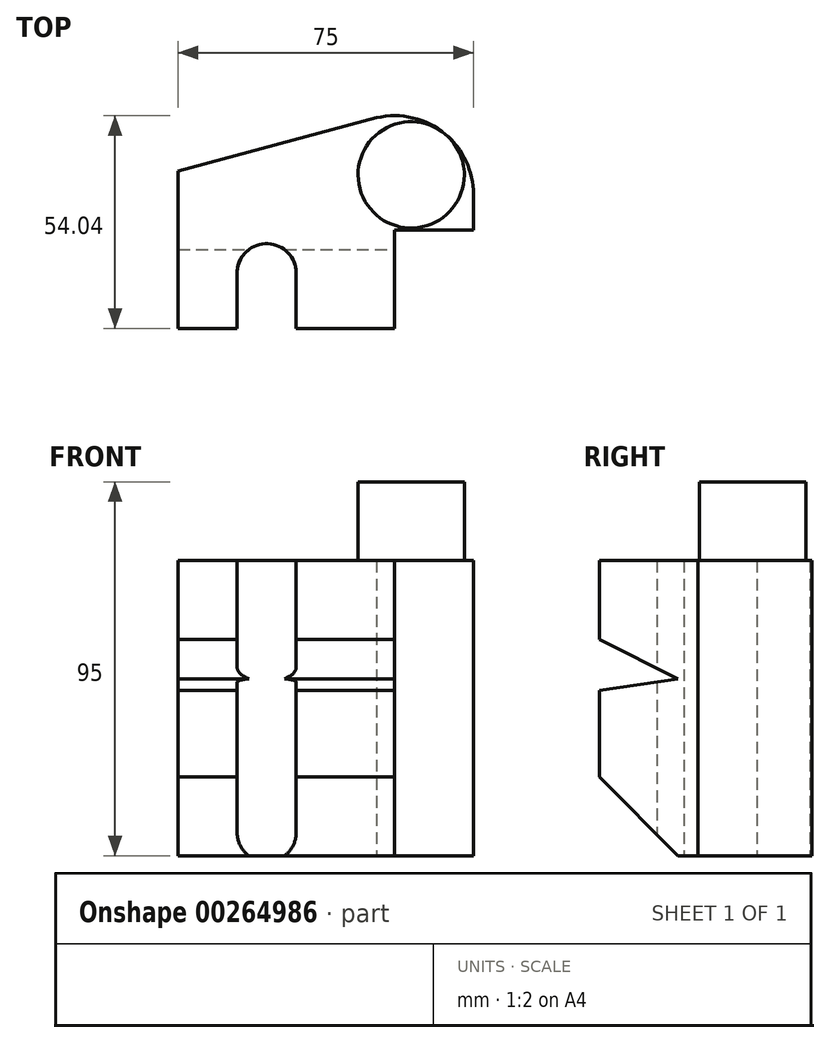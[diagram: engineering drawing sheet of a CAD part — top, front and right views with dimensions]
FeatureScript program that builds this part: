
annotation { "Feature Type Name" : "Feature", "Feature Type Description" : "" }
export const myFeature = defineFeature(function(context is Context, id is Id, definition is map)
    precondition{}
    {
        {
            var Q0;
            Q0=qCreatedBy(makeId("Top.planeOp"),FACE);
            var sketch = newSketch(context, id + "F0", { "sketchPlane" : qUnion([Q0])});
            skLineSegment(sketch, "E0", {"start": v(0, 0) * mm, "end": v(15, 0) * mm});
            skLineSegment(sketch, "E1", {"start": v(15, 0) * mm, "end": v(15, 14.68) * mm});
            skLineSegment(sketch, "E2", {"start": v(30, 14) * mm, "end": v(30, 0) * mm});
            skLineSegment(sketch, "E3", {"start": v(30, 0) * mm, "end": v(55, 0) * mm});
            skLineSegment(sketch, "E4", {"start": v(55, 0) * mm, "end": v(55, 25) * mm});
            skLineSegment(sketch, "E5", {"start": v(55, 25) * mm, "end": v(75, 25) * mm});
            skLineSegment(sketch, "E6", {"start": v(75, 25) * mm, "end": v(75, 34.04) * mm});
            skLineSegment(sketch, "E7", {"start": v(0, 0) * mm, "end": v(0, 40) * mm});
            skLineSegment(sketch, "E8", {"start": v(0, 40) * mm, "end": v(50.41, 53.5) * mm});
            skArc(sketch, "E9", {"start": v(30, 14) * mm, "mid": v(22.82, 21.5) * mm, "end": v(15, 14.68) * mm});
            skArc(sketch, "E10", {"start": v(75, 34.04) * mm, "mid": v(67.42, 49.72) * mm, "end": v(50.41, 53.5) * mm});
            skSolve(sketch);
        }
        {
            var Q0;
            Q0 = qSketchRegion(id + "F0", true);
            extrude(context, id + "F1", {"entities" : qUnion([Q0]), "depth" : 75 * mm});
        }
        {
            var Q0;
            Q0=makeQuery(id+"F1.opExtrude","CAP_FACE",FACE,{"disambiguationData":[OSD([sQuery(id+"F0.wireOp",EDGE,"E0"),sQuery(id+"F0.wireOp",EDGE,"E1"),sQuery(id+"F0.wireOp",EDGE,"E2"),sQuery(id+"F0.wireOp",EDGE,"E3"),sQuery(id+"F0.wireOp",EDGE,"E4"),sQuery(id+"F0.wireOp",EDGE,"E5"),sQuery(id+"F0.wireOp",EDGE,"E6"),sQuery(id+"F0.wireOp",EDGE,"E7"),sQuery(id+"F0.wireOp",EDGE,"E8"),sQuery(id+"F0.wireOp",EDGE,"E9"),sQuery(id+"F0.wireOp",EDGE,"E10")])],"isStart":false});
            var sketch = newSketch(context, id + "F2", { "sketchPlane" : qUnion([Q0])});
            skCircle(sketch, "E11", {"center": v(59.2, 39) * mm, "radius": 13.5 * mm});
            skSolve(sketch);
        }
        {
            var Q0;
            Q0 = qSketchRegion(id + "F2", true);
            extrude(context, id + "F3", {"entities" : qUnion([Q0]), "operationType" : NewBodyOperationType.ADD, "depth" : 20 * mm});
        }
        {
            var Q0;
            Q0=makeQuery(id+"F1.opExtrude","SWEPT_FACE",FACE,{"disambiguationData":[OSD([sQuery(id+"F0.wireOp",EDGE,"E4")])]});
            var sketch = newSketch(context, id + "F4", { "sketchPlane" : qUnion([Q0])});
            skLineSegment(sketch, "E12", {"start": v(0, 55) * mm, "end": v(20, 45) * mm});
            skLineSegment(sketch, "E13", {"start": v(20, 45) * mm, "end": v(0, 42.03) * mm});
            skLineSegment(sketch, "E14", {"start": v(0, 42.03) * mm, "end": v(0, 55) * mm});
            skSolve(sketch);
        }
        {
            var Q0;
            Q0 = qSketchRegion(id + "F4", true);
            extrude(context, id + "F5", {"entities" : qUnion([Q0]), "operationType" : NewBodyOperationType.REMOVE, "endBound" : BoundingType.THROUGH_ALL, "oppositeDirection" : true, "depth" : 25 * mm});
        }
        {
            var Q0;
            Q0=makeQuery(id+"F1.opExtrude","SWEPT_FACE",FACE,{"disambiguationData":[OSD([sQuery(id+"F0.wireOp",EDGE,"E4")])]});
            var sketch = newSketch(context, id + "F6", { "sketchPlane" : qUnion([Q0])});
            skLineSegment(sketch, "E15", {"start": v(0, 20) * mm, "end": v(20, 0) * mm});
            skLineSegment(sketch, "E16", {"start": v(20, 0) * mm, "end": v(0, 0) * mm});
            skLineSegment(sketch, "E17", {"start": v(0, 0) * mm, "end": v(0, 20) * mm});
            skSolve(sketch);
        }
        {
            var Q0;
            Q0 = qSketchRegion(id + "F6", true);
            extrude(context, id + "F7", {"entities" : qUnion([Q0]), "operationType" : NewBodyOperationType.REMOVE, "endBound" : BoundingType.THROUGH_ALL, "oppositeDirection" : true, "depth" : 25 * mm});
        }
    });
